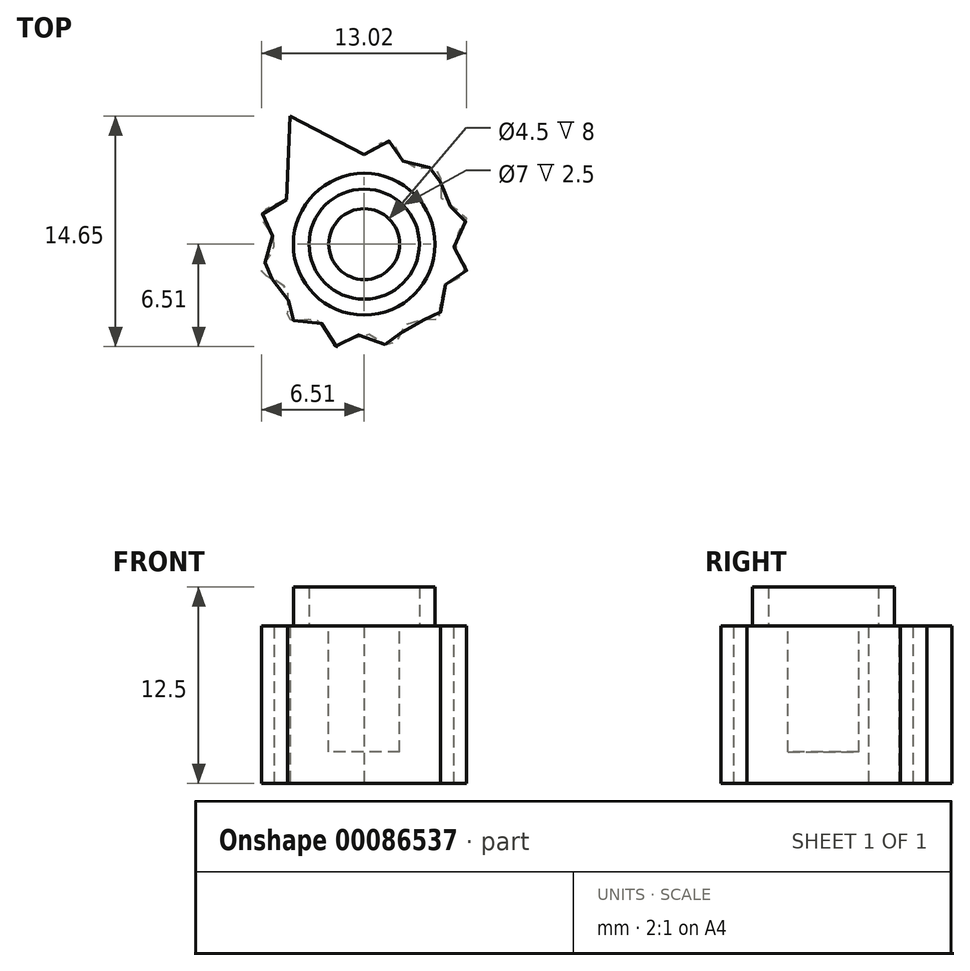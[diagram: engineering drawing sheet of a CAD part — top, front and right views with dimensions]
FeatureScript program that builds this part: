
annotation { "Feature Type Name" : "Feature", "Feature Type Description" : "" }
export const myFeature = defineFeature(function(context is Context, id is Id, definition is map)
    precondition{}
    {
        {
            var Q0;
            Q0=qCreatedBy(makeId("Top.planeOp"),FACE);
            var sketch = newSketch(context, id + "F0", { "sketchPlane" : qUnion([Q0])});
            skCircle(sketch, "E0.cCircle", {"center": v(0, 0) * mm, "radius": 6.5 * mm, "construction": true});
            skLineSegment(sketch, "E0.0", {"start": v(-1.74, 6.5) * mm, "end": v(1.74, 6.5) * mm, "construction": true});
            skLineSegment(sketch, "E0.1", {"start": v(1.74, 6.5) * mm, "end": v(4.76, 4.76) * mm, "construction": true});
            skLineSegment(sketch, "E0.2", {"start": v(4.76, 4.76) * mm, "end": v(6.5, 1.74) * mm, "construction": true});
            skLineSegment(sketch, "E0.3", {"start": v(6.5, 1.74) * mm, "end": v(6.5, -1.74) * mm, "construction": true});
            skLineSegment(sketch, "E0.4", {"start": v(6.5, -1.74) * mm, "end": v(4.76, -4.76) * mm, "construction": true});
            skLineSegment(sketch, "E0.5", {"start": v(4.76, -4.76) * mm, "end": v(1.74, -6.5) * mm, "construction": true});
            skLineSegment(sketch, "E0.6", {"start": v(1.74, -6.5) * mm, "end": v(-1.74, -6.5) * mm, "construction": true});
            skLineSegment(sketch, "E0.7", {"start": v(-1.74, -6.5) * mm, "end": v(-4.76, -4.76) * mm, "construction": true});
            skLineSegment(sketch, "E0.8", {"start": v(-4.76, -4.76) * mm, "end": v(-6.5, -1.74) * mm, "construction": true});
            skLineSegment(sketch, "E0.9", {"start": v(-6.5, -1.74) * mm, "end": v(-6.5, 1.74) * mm, "construction": true});
            skLineSegment(sketch, "E0.10", {"start": v(-6.5, 1.74) * mm, "end": v(-4.76, 4.76) * mm, "construction": true});
            skLineSegment(sketch, "E0.11", {"start": v(-4.76, 4.76) * mm, "end": v(-1.74, 6.5) * mm, "construction": true});
            skPoint(sketch, "E0.0.midPoint", {"position": v(0, 6.5) * mm});
            skCircle(sketch, "E1.cCircle", {"center": v(0, 0) * mm, "radius": 5.5 * mm, "construction": true});
            skLineSegment(sketch, "E1.0", {"start": v(0, 5.7) * mm, "end": v(2.85, 4.93) * mm, "construction": true});
            skLineSegment(sketch, "E1.1", {"start": v(2.85, 4.93) * mm, "end": v(4.93, 2.85) * mm, "construction": true});
            skLineSegment(sketch, "E1.2", {"start": v(4.93, 2.85) * mm, "end": v(5.7, 0) * mm, "construction": true});
            skLineSegment(sketch, "E1.3", {"start": v(5.7, 0) * mm, "end": v(4.93, -2.85) * mm, "construction": true});
            skLineSegment(sketch, "E1.4", {"start": v(4.93, -2.85) * mm, "end": v(2.85, -4.93) * mm, "construction": true});
            skLineSegment(sketch, "E1.5", {"start": v(2.85, -4.93) * mm, "end": v(0, -5.7) * mm, "construction": true});
            skLineSegment(sketch, "E1.6", {"start": v(0, -5.7) * mm, "end": v(-2.85, -4.93) * mm, "construction": true});
            skLineSegment(sketch, "E1.7", {"start": v(-2.85, -4.93) * mm, "end": v(-4.93, -2.85) * mm, "construction": true});
            skLineSegment(sketch, "E1.8", {"start": v(-4.93, -2.85) * mm, "end": v(-5.7, 0) * mm, "construction": true});
            skLineSegment(sketch, "E1.9", {"start": v(-5.7, 0) * mm, "end": v(-4.93, 2.85) * mm, "construction": true});
            skLineSegment(sketch, "E1.10", {"start": v(-4.93, 2.85) * mm, "end": v(-2.85, 4.93) * mm, "construction": true});
            skLineSegment(sketch, "E1.11", {"start": v(-2.85, 4.93) * mm, "end": v(0, 5.7) * mm, "construction": true});
            skPoint(sketch, "E1.0.midPoint", {"position": v(1.42, 5.31) * mm});
            skFitSpline(sketch, "E2", {"points": [v(0, 5.7) * mm, v(1.74, 6.5) * mm, v(2.85, 4.93) * mm, v(4.76, 4.76) * mm, v(4.93, 2.85) * mm, v(6.5, 1.74) * mm, v(5.7, 0) * mm, v(6.5, -1.74) * mm, v(4.93, -2.85) * mm, v(4.76, -4.76) * mm, v(2.85, -4.93) * mm, v(1.74, -6.5) * mm, v(0, -5.7) * mm, v(-1.74, -6.5) * mm, v(-2.85, -4.93) * mm, v(-4.76, -4.76) * mm, v(-4.93, -2.85) * mm, v(-6.5, -1.74) * mm, v(-5.7, 0) * mm, v(-6.5, 1.74) * mm, v(-4.93, 2.85) * mm], "startDerivative": vector(40.3, 31.62) * mm, "endDerivative": vector(47.53, 19.09) * mm});
            skLineSegment(sketch, "E3", {"start": v(-4.93, 2.85) * mm, "end": v(-4.7, 8.14) * mm});
            skLineSegment(sketch, "E4", {"start": v(-4.7, 8.14) * mm, "end": v(0, 5.7) * mm});
            skSolve(sketch);
        }
        {
            var Q0;
            Q0 = qSketchRegion(id + "F0", true);
            extrude(context, id + "F1", {"entities" : qUnion([Q0]), "depth" : 10 * mm});
        }
        {
            var Q0;
            Q0=makeQuery(id+"F1.opExtrude","CAP_FACE",FACE,{"disambiguationData":[OSD([sQuery(id+"F0.wireOp",EDGE,"E2"),sQuery(id+"F0.wireOp",EDGE,"E3"),sQuery(id+"F0.wireOp",EDGE,"E4")])],"isStart":false});
            var sketch = newSketch(context, id + "F2", { "sketchPlane" : qUnion([Q0])});
            skCircle(sketch, "E5", {"center": v(0, 0) * mm, "radius": 2.25 * mm});
            skCircle(sketch, "E6", {"center": v(0, 0) * mm, "radius": 3.5 * mm});
            skCircle(sketch, "E7", {"center": v(0, 0) * mm, "radius": 4.5 * mm});
            skSolve(sketch);
        }
        {
            var Q0;
            Q0=makeQuery(id+"F2.imprint","IMPRINT",FACE,{"disambiguationData":[TD([[makeQuery(id+"F2.imprint","IMPRINT",EDGE,{"derivedFrom":sQuery(id+"F2.wireOp",EDGE,"E5")}),1.0]])]});
            extrude(context, id + "F3", {"entities" : qUnion([Q0]), "operationType" : NewBodyOperationType.REMOVE, "oppositeDirection" : true, "depth" : 8 * mm});
        }
        {
            var Q0;
            Q0=makeQuery(id+"F2.imprint","IMPRINT",FACE,{"disambiguationData":[TD([[makeQuery(id+"F2.imprint","IMPRINT",EDGE,{"derivedFrom":sQuery(id+"F2.wireOp",EDGE,"E6")}),-1.0]])]});
            extrude(context, id + "F4", {"entities" : qUnion([Q0]), "operationType" : NewBodyOperationType.ADD, "depth" : 2.5 * mm});
        }
    });
